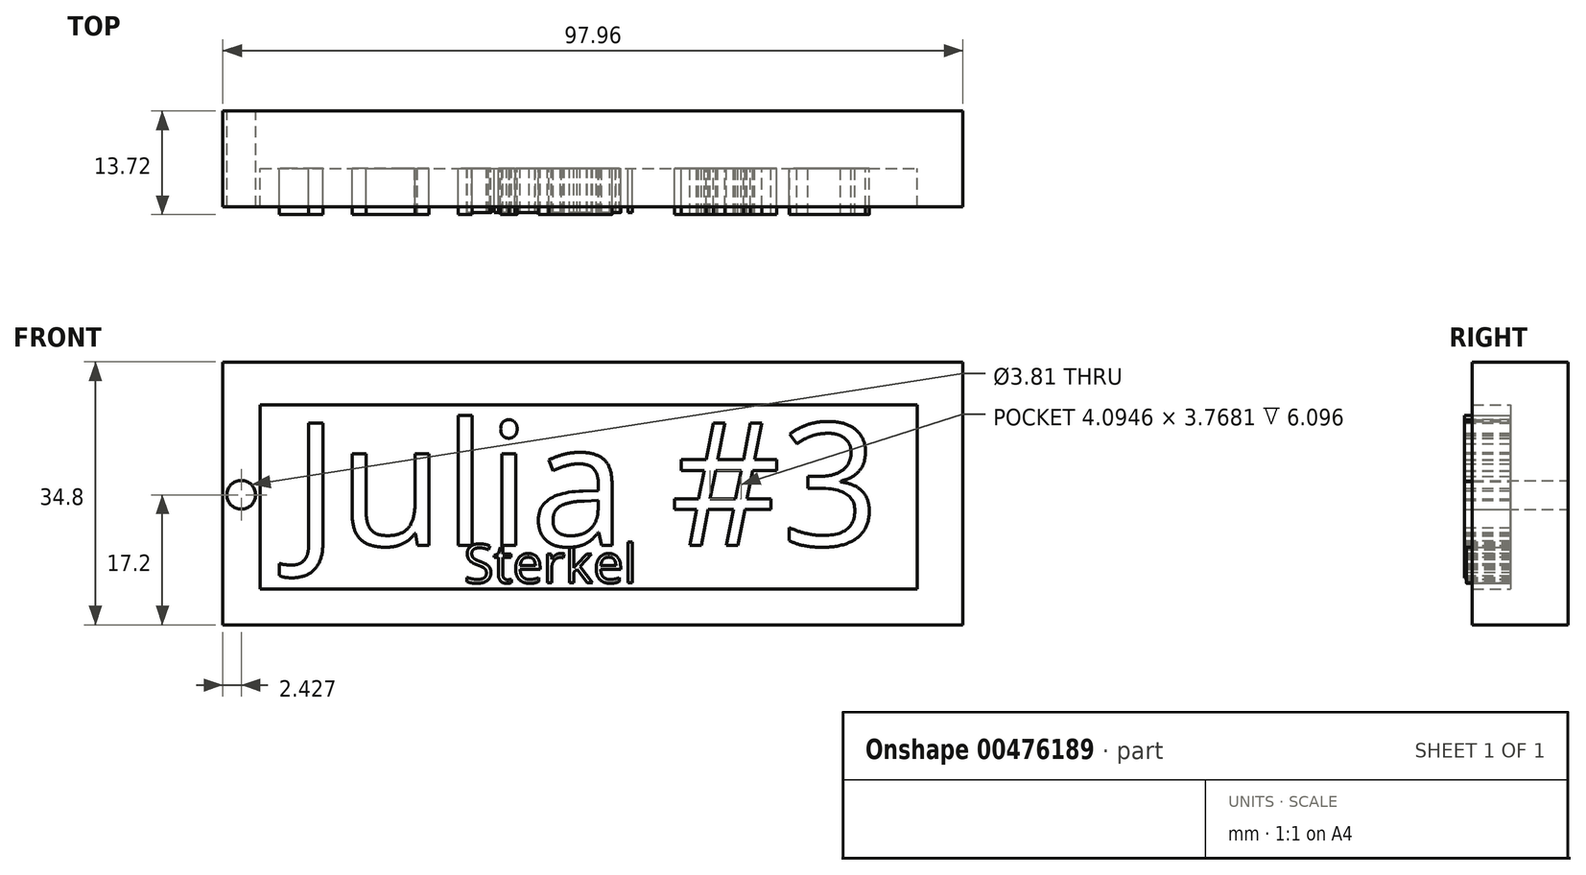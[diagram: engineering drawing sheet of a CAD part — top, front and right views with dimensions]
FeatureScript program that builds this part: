
annotation { "Feature Type Name" : "Feature", "Feature Type Description" : "" }
export const myFeature = defineFeature(function(context is Context, id is Id, definition is map)
    precondition{}
    {
        {
            var Q0;
            Q0=qCreatedBy(makeId("Front.planeOp"),FACE);
            var sketch = newSketch(context, id + "F0", { "sketchPlane" : qUnion([Q0])});
            skLineSegment(sketch, "E0.bottom", {"start": v(-53.39, 17.6) * mm, "end": v(44.57, 17.6) * mm});
            skLineSegment(sketch, "E0.top", {"start": v(-53.39, -17.2) * mm, "end": v(44.57, -17.2) * mm});
            skLineSegment(sketch, "E0.left", {"start": v(-53.39, 17.6) * mm, "end": v(-53.39, -17.2) * mm});
            skLineSegment(sketch, "E0.right", {"start": v(44.57, 17.6) * mm, "end": v(44.57, -17.2) * mm});
            skLineSegment(sketch, "E1.bottom", {"start": v(-48.45, 11.88) * mm, "end": v(38.55, 11.88) * mm});
            skLineSegment(sketch, "E1.top", {"start": v(-48.45, -12.5) * mm, "end": v(38.55, -12.5) * mm});
            skLineSegment(sketch, "E1.left", {"start": v(-48.45, 11.88) * mm, "end": v(-48.45, -12.5) * mm});
            skLineSegment(sketch, "E1.right", {"start": v(38.55, 11.88) * mm, "end": v(38.55, -12.5) * mm});
            skSolve(sketch);
        }
        {
            var Q0;
            Q0=makeQuery(id+"F0.imprint","IMPRINT",FACE,{"disambiguationData":[TD([[makeQuery(id+"F0.imprint","IMPRINT",EDGE,{"derivedFrom":sQuery(id+"F0.wireOp",EDGE,"E0.bottom")}),-1.0]])]});
            extrude(context, id + "F1", {"entities" : qUnion([Q0]), "depth" : 12.7 * mm});
        }
        {
            var Q0;
            Q0=qCreatedBy(makeId("Front.planeOp"),FACE);
            var sketch = newSketch(context, id + "F2", { "sketchPlane" : qUnion([Q0])});
            skLineSegment(sketch, "E2.bottom", {"start": v(38.61, 11.97) * mm, "end": v(-48.66, 11.97) * mm});
            skLineSegment(sketch, "E2.top", {"start": v(38.61, -13.06) * mm, "end": v(-48.66, -13.06) * mm});
            skLineSegment(sketch, "E2.left", {"start": v(38.61, 11.97) * mm, "end": v(38.61, -13.06) * mm});
            skLineSegment(sketch, "E2.right", {"start": v(-48.66, 11.97) * mm, "end": v(-48.66, -13.06) * mm});
            skSolve(sketch);
        }
        {
            var Q0;
            Q0=makeQuery(id+"F2.imprint","IMPRINT",FACE,{"disambiguationData":[TD([[makeQuery(id+"F2.imprint","IMPRINT",EDGE,{"derivedFrom":sQuery(id+"F2.wireOp",EDGE,"E2.bottom")}),1.0]])]});
            extrude(context, id + "F3", {"entities" : qUnion([Q0]), "operationType" : NewBodyOperationType.ADD, "depth" : 7.62 * mm});
        }
        {
            var Q0;
            Q0=qCreatedBy(makeId("Front.planeOp"),FACE);
            var sketch = newSketch(context, id + "F4", { "sketchPlane" : qUnion([Q0])});
            skText(sketch, "E3", { "text": "Julia #3", "fontName": "OpenSans-Regular.ttf"});
            const initialGuessF4  = {"E3": [-0.04416, -0.00672, 1, 0, 0.01635]};
            skSetInitialGuess(sketch, initialGuessF4);
            skSolve(sketch);
        }
        {
            var Q0;
            Q0 = qSketchRegion(id + "F4", true);
            extrude(context, id + "F5", {"entities" : qUnion([Q0]), "operationType" : NewBodyOperationType.ADD, "depth" : 13.72 * mm});
        }
        {
            var Q0;
            Q0=qCreatedBy(makeId("Front.planeOp"),FACE);
            var sketch = newSketch(context, id + "F6", { "sketchPlane" : qUnion([Q0])});
            skPoint(sketch, "E4", {"position": v(-50.96, 0) * mm});
            skSolve(sketch);
        }
        {
            var Q0;
            Q0=sQuery(id+"F6.wireOp",VERTEX,"E4");
            var Q1;
            Q1=makeQuery(id+"F1.opExtrude","SWEPT_BODY",BODY,{"disambiguationData":[OSD([sQuery(id+"F0.wireOp",EDGE,"E0.bottom"),sQuery(id+"F0.wireOp",EDGE,"E0.top"),sQuery(id+"F0.wireOp",EDGE,"E0.left"),sQuery(id+"F0.wireOp",EDGE,"E0.right"),sQuery(id+"F0.wireOp",EDGE,"E1.bottom"),sQuery(id+"F0.wireOp",EDGE,"E1.top"),sQuery(id+"F0.wireOp",EDGE,"E1.left"),sQuery(id+"F0.wireOp",EDGE,"E1.right")])]});
            hole(context, id + "F7", {"style" : HoleStyle.SIMPLE, "endStyle" : HoleEndStyle.THROUGH, "oppositeDirection" : true, "holeDiameter" : 3.8 * mm, "isTappedThrough" : true, "tappedDepth" : 12.7 * mm, "tapClearance" : 3, "locations" : qUnion([Q0]), "scope" : qUnion([Q1])});
        }
        {
            var Q0;
            Q0=qCreatedBy(makeId("Front.planeOp"),FACE);
            var sketch = newSketch(context, id + "F8", { "sketchPlane" : qUnion([Q0])});
            skText(sketch, "E5", { "text": "Sterkel", "fontName": "OpenSans-Regular.ttf"});
            const initialGuessF8  = {"E5": [-0.02148, -0.01165, 1, 0, 0.00514]};
            skSetInitialGuess(sketch, initialGuessF8);
            skSolve(sketch);
        }
        {
            var Q0;
            Q0 = qSketchRegion(id + "F8", true);
            extrude(context, id + "F9", {"entities" : qUnion([Q0]), "operationType" : NewBodyOperationType.ADD, "depth" : 13.46 * mm});
        }
    });
